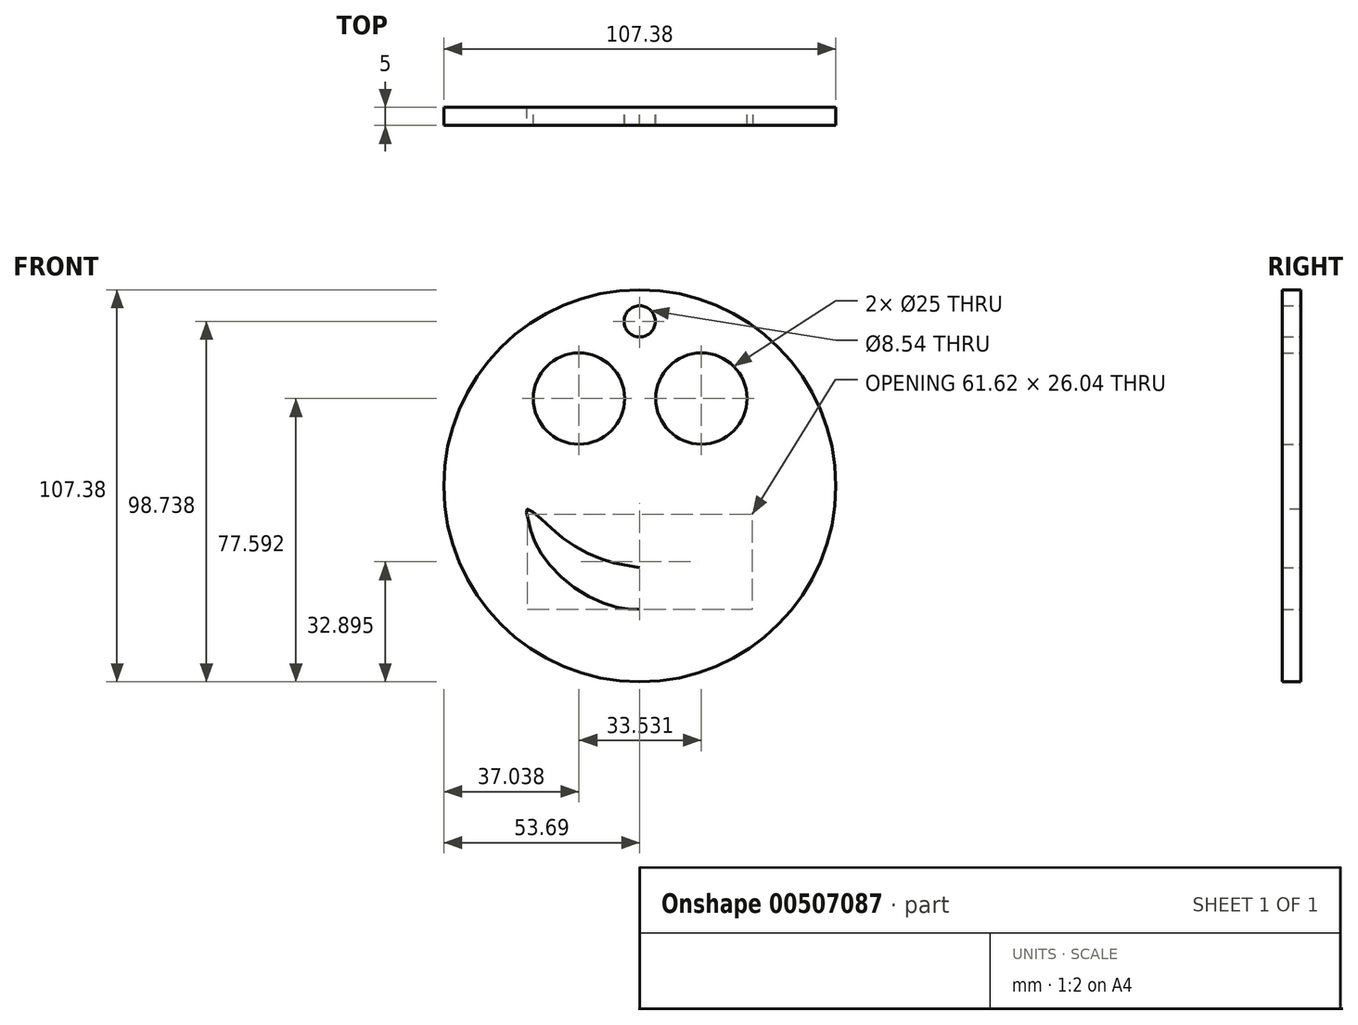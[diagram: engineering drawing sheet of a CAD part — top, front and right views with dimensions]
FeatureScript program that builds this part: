
annotation { "Feature Type Name" : "Feature", "Feature Type Description" : "" }
export const myFeature = defineFeature(function(context is Context, id is Id, definition is map)
    precondition{}
    {
        {
            var Q0;
            Q0=qCreatedBy(makeId("Front.planeOp"),FACE);
            var sketch = newSketch(context, id + "F0", { "sketchPlane" : qUnion([Q0])});
            skCircle(sketch, "E0", {"center": v(0, 0) * mm, "radius": 53.7 * mm});
            skCircle(sketch, "E1", {"center": v(-16.65, 23.9) * mm, "radius": 12.5 * mm});
            skCircle(sketch, "E2", {"center": v(16.88, 23.9) * mm, "radius": 12.5 * mm});
            skPoint(sketch, "E3.MirrorCS.end.orphan", {"position": v(0, -33.81) * mm});
            skPoint(sketch, "E3.MirrorCS.start.orphan", {"position": v(0, -16.29) * mm});
            skFitSpline(sketch, "E4", {"points": [v(0, -22.36) * mm, v(-10.45, -20.1) * mm, v(-21.68, -13.82) * mm, v(-29.32, -7.08) * mm, v(-30.9, -6.4) * mm, v(-30.9, -7.75) * mm, v(-29.32, -13.82) * mm, v(-22.58, -23.93) * mm, v(-9.1, -32.47) * mm, v(0, -33.81) * mm], "startDerivative": vector(-81.25, 12.05) * mm, "endDerivative": vector(72.5, -2.6) * mm});
            skFitSpline(sketch, "E5.MirrorCS", {"points": [v(0, -22.36) * mm, v(10.45, -20.1) * mm, v(21.68, -13.82) * mm, v(29.32, -7.08) * mm, v(30.9, -6.4) * mm, v(30.9, -7.75) * mm, v(29.32, -13.82) * mm, v(22.58, -23.93) * mm, v(9.1, -32.47) * mm, v(0, -33.81) * mm], "startDerivative": vector(81.25, 12.05) * mm, "endDerivative": vector(-72.5, -2.6) * mm});
            skFitSpline(sketch, "E6.MirrorCS", {"points": [v(0, -22.36) * mm, v(10.45, -20.1) * mm, v(21.68, -13.82) * mm, v(29.32, -7.08) * mm, v(30.9, -6.4) * mm, v(30.9, -7.75) * mm, v(29.32, -13.82) * mm, v(22.58, -23.93) * mm, v(9.1, -32.47) * mm, v(0, -33.81) * mm], "startDerivative": vector(81.25, 12.05) * mm, "endDerivative": vector(-72.5, -2.6) * mm});
            skCircle(sketch, "E7", {"center": v(0, 45.05) * mm, "radius": 4.27 * mm});
            skPoint(sketch, "E8.1.internal.orphan", {"position": v(-14.72, 14.04) * mm});
            skPoint(sketch, "E8.2.internal.orphan", {"position": v(-14.5, 16.51) * mm});
            skPoint(sketch, "E8.3.internal.orphan", {"position": v(-15.09, 17.81) * mm});
            skPoint(sketch, "E9.1.internal.orphan", {"position": v(-18.54, 14.04) * mm});
            skPoint(sketch, "E9.2.internal.orphan", {"position": v(-18.76, 16.51) * mm});
            skPoint(sketch, "E9.endDerivative.orphan", {"position": v(-19.35, 17.81) * mm});
            skSolve(sketch);
        }
        {
            var Q0;
            Q0 = qSketchRegion(id + "F0", true);
            extrude(context, id + "F1", {"entities" : qUnion([Q0]), "depth" : 5 * mm});
        }
    });
